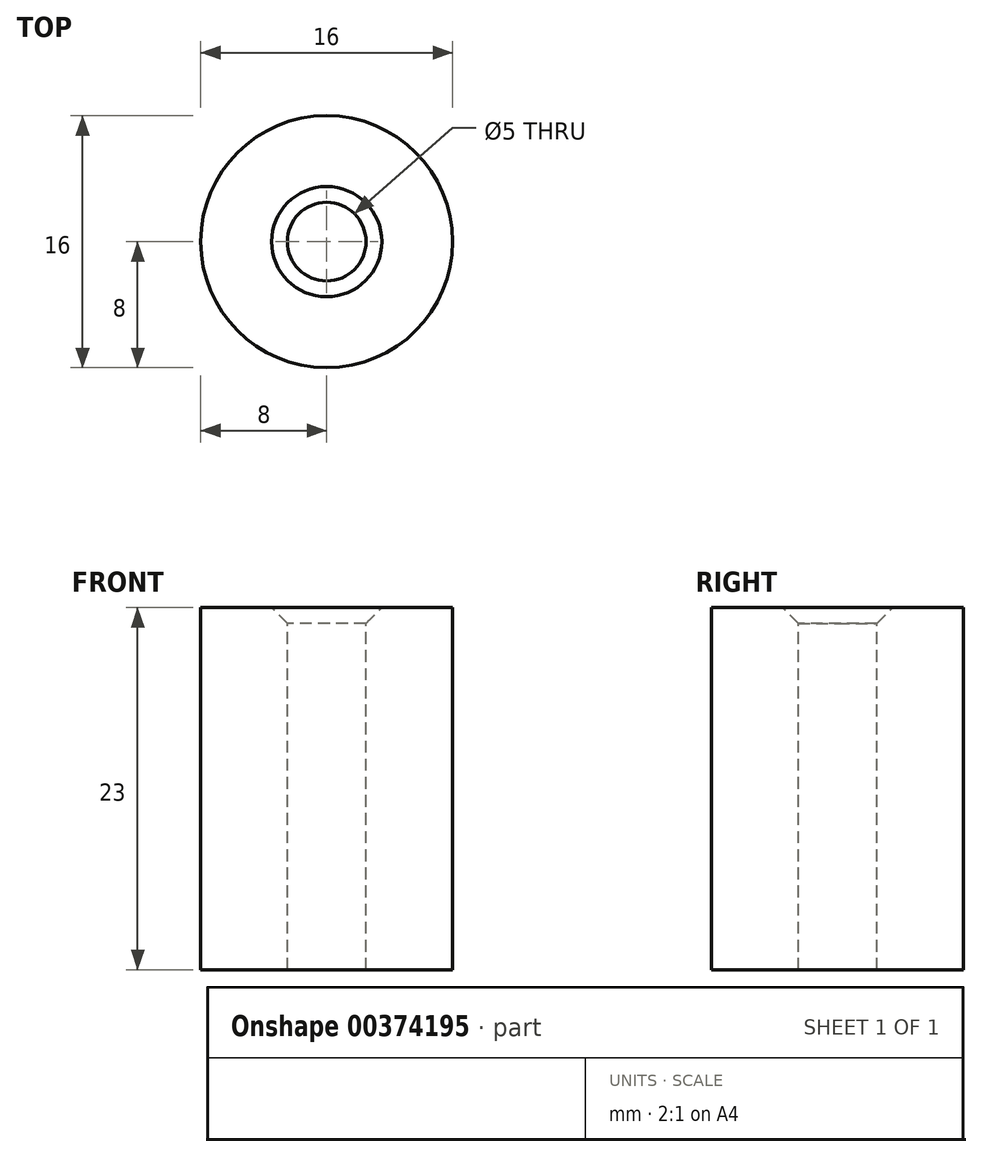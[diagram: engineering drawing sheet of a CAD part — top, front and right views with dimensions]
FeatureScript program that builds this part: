
annotation { "Feature Type Name" : "Feature", "Feature Type Description" : "" }
export const myFeature = defineFeature(function(context is Context, id is Id, definition is map)
    precondition{}
    {
        {
            var Q0;
            Q0=qCreatedBy(makeId("Top.planeOp"),FACE);
            var sketch = newSketch(context, id + "F0", { "sketchPlane" : qUnion([Q0])});
            skCircle(sketch, "E0", {"center": v(0, 0) * mm, "radius": 8 * mm});
            skSolve(sketch);
        }
        {
            var Q0;
            Q0 = qSketchRegion(id + "F0", true);
            extrude(context, id + "F1", {"entities" : qUnion([Q0]), "oppositeDirection" : true, "depth" : 23 * mm});
        }
        {
            var Q0;
            Q0=makeQuery(id+"F1.opExtrude","CAP_FACE",FACE,{"disambiguationData":[OSD([sQuery(id+"F0.wireOp",EDGE,"E0")])],"isStart":true});
            var Q1;
            Q1=makeQuery(id+"F1.opExtrude","CAP_FACE",FACE,{"disambiguationData":[OSD([sQuery(id+"F0.wireOp",EDGE,"E0")])],"isStart":false});
            var Q2;
            Q2=makeQuery(id+"F1.opExtrude","SWEPT_BODY",BODY,{"disambiguationData":[OSD([sQuery(id+"F0.wireOp",EDGE,"E0")])]});
            shell(context, id + "F2", {"entities" : qUnion([Q0, Q1]), "parts" : qUnion([Q2]), "thickness" : 5.5 * mm});
        }
        {
            var Q0;
            {var subQ0=sQuery(id+"F0.wireOp",EDGE,"E0");Q0=makeQuery(id+"F2.opShell","OFFSET_EDGE",EDGE,{"disambiguationData":[OSD([subQ0]),TDD([makeQuery(id+"F1.opExtrude","CAP_EDGE",EDGE,{"disambiguationData":[OSD([subQ0])],"isStart":true})])]});}
            chamfer(context, id + "F3", {"entities" : qUnion([Q0]), "width" : 1 * mm, "tangentPropagation" : true});
        }
    });
